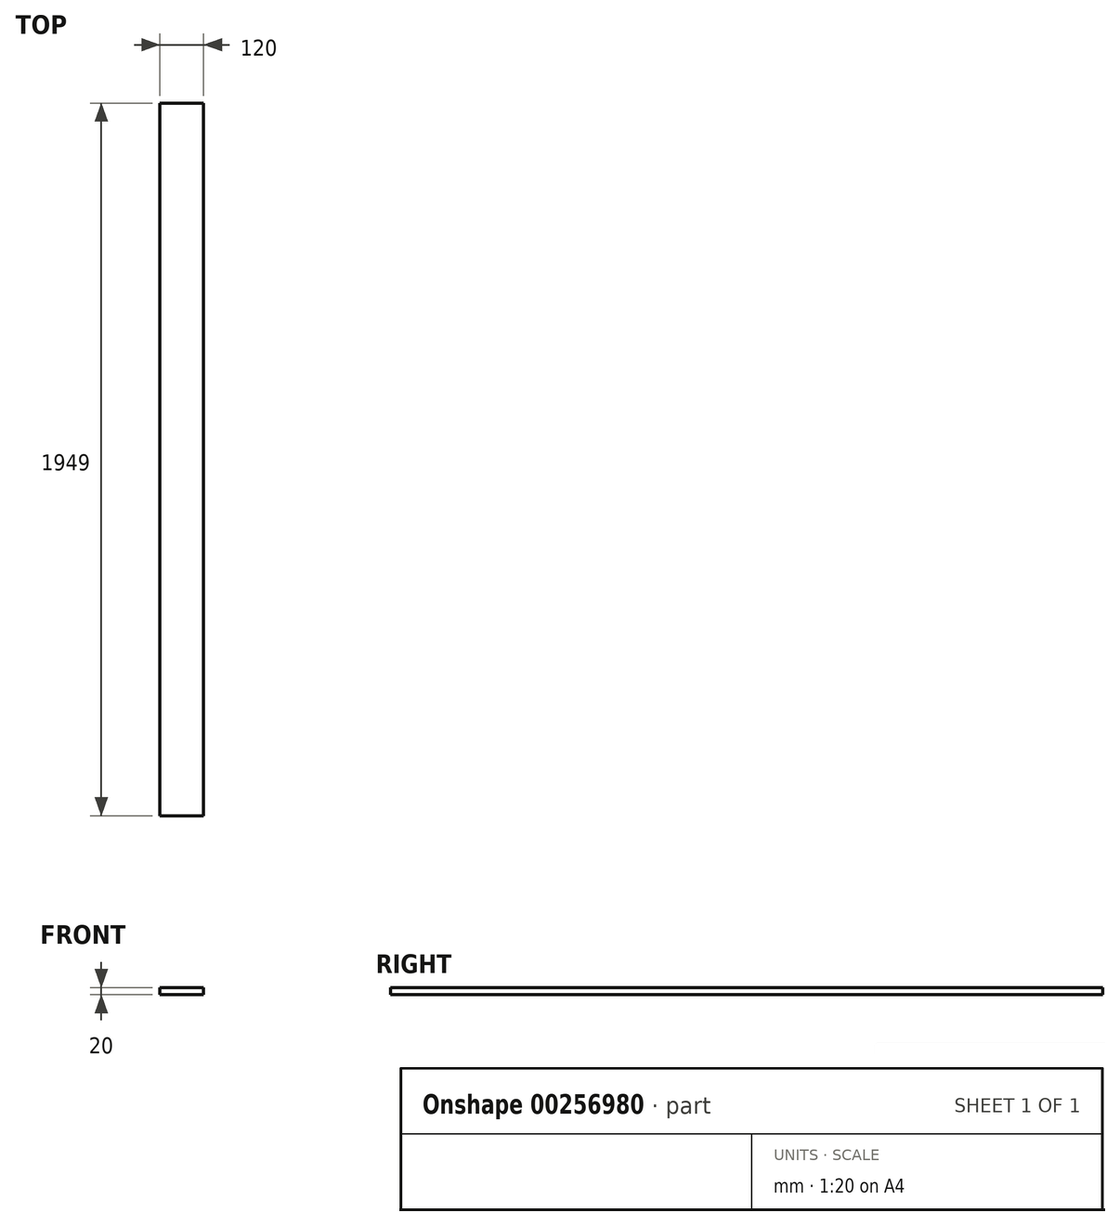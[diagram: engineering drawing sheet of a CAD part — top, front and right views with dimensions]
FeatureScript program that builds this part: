
annotation { "Feature Type Name" : "Feature", "Feature Type Description" : "" }
export const myFeature = defineFeature(function(context is Context, id is Id, definition is map)
    precondition{}
    {
        {
            var Q0;
            Q0=qCreatedBy(makeId("Front.planeOp"),FACE);
            var sketch = newSketch(context, id + "F0", { "sketchPlane" : qUnion([Q0])});
            skLineSegment(sketch, "E0.bottom", {"start": v(0, 0) * mm, "end": v(120, 0) * mm});
            skLineSegment(sketch, "E0.top", {"start": v(0, 20) * mm, "end": v(120, 20) * mm});
            skLineSegment(sketch, "E0.left", {"start": v(0, 0) * mm, "end": v(0, 20) * mm});
            skLineSegment(sketch, "E0.right", {"start": v(120, 0) * mm, "end": v(120, 20) * mm});
            skSolve(sketch);
        }
        {
            var Q0;
            Q0=makeQuery(id+"F0.imprint","IMPRINT",FACE,{"disambiguationData":[TD([[makeQuery(id+"F0.imprint","IMPRINT",EDGE,{"derivedFrom":sQuery(id+"F0.wireOp",EDGE,"E0.bottom")}),1.0]])]});
            extrude(context, id + "F1", {"entities" : qUnion([Q0]), "depth" : 1949 * mm});
        }
    });
